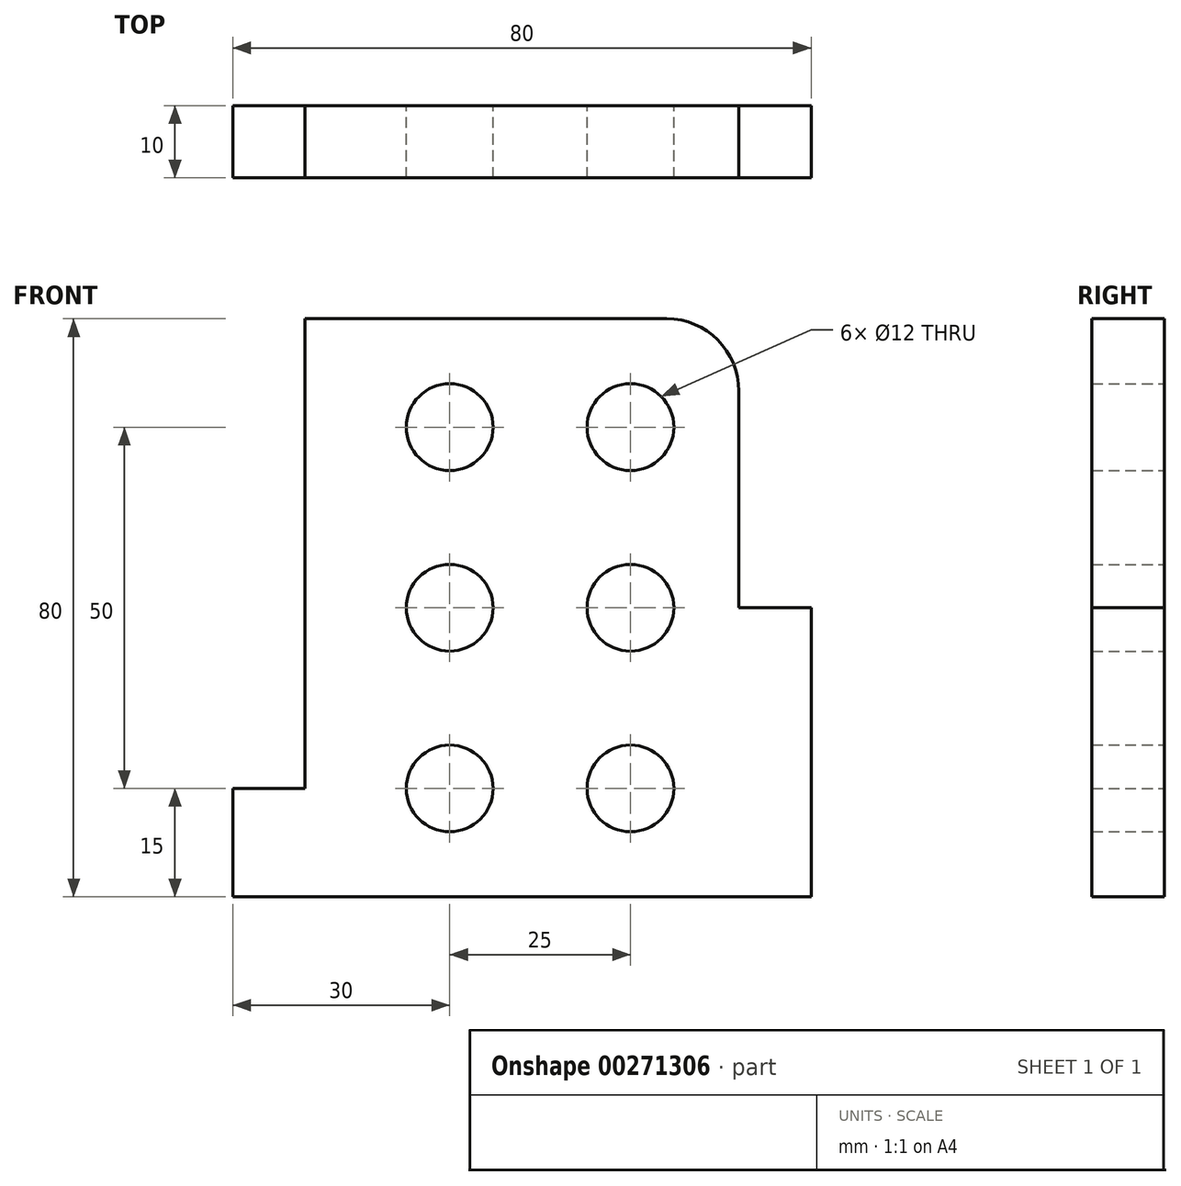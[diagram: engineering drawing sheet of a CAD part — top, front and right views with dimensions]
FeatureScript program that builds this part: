
annotation { "Feature Type Name" : "Feature", "Feature Type Description" : "" }
export const myFeature = defineFeature(function(context is Context, id is Id, definition is map)
    precondition{}
    {
        {
            var Q0;
            Q0=qCreatedBy(makeId("Front.planeOp"),FACE);
            var sketch = newSketch(context, id + "F0", { "sketchPlane" : qUnion([Q0])});
            skLineSegment(sketch, "E0", {"start": v(0, 0) * mm, "end": v(0, 15) * mm});
            skLineSegment(sketch, "E1", {"start": v(0, 15) * mm, "end": v(10, 15) * mm});
            skLineSegment(sketch, "E2", {"start": v(10, 15) * mm, "end": v(10, 80) * mm});
            skLineSegment(sketch, "E3", {"start": v(10, 80) * mm, "end": v(60, 80) * mm});
            skCircle(sketch, "E4", {"center": v(30, 15) * mm, "radius": 6 * mm});
            skCircle(sketch, "E5", {"center": v(55, 15) * mm, "radius": 6 * mm});
            skCircle(sketch, "E6", {"center": v(55, 40) * mm, "radius": 6 * mm});
            skCircle(sketch, "E7", {"center": v(30, 40) * mm, "radius": 6 * mm});
            skCircle(sketch, "E8", {"center": v(30, 65) * mm, "radius": 6 * mm});
            skCircle(sketch, "E9", {"center": v(55, 65) * mm, "radius": 6 * mm});
            skLineSegment(sketch, "E10", {"start": v(0, 0) * mm, "end": v(80, 0) * mm});
            skLineSegment(sketch, "E11", {"start": v(80, 0) * mm, "end": v(80, 40) * mm});
            skLineSegment(sketch, "E12", {"start": v(80, 40) * mm, "end": v(70, 40) * mm});
            skLineSegment(sketch, "E13", {"start": v(70, 40) * mm, "end": v(70, 70) * mm});
            skArc(sketch, "E14", {"start": v(70, 70) * mm, "mid": v(67.07, 77.07) * mm, "end": v(60, 80) * mm});
            skLineSegment(sketch, "E15.bottom", {"start": v(30, 65) * mm, "end": v(55, 65) * mm, "construction": true});
            skLineSegment(sketch, "E15.top", {"start": v(30, 15) * mm, "end": v(55, 15) * mm, "construction": true});
            skLineSegment(sketch, "E15.left", {"start": v(30, 65) * mm, "end": v(30, 15) * mm, "construction": true});
            skLineSegment(sketch, "E15.right", {"start": v(55, 65) * mm, "end": v(55, 15) * mm, "construction": true});
            skLineSegment(sketch, "E16", {"start": v(30, 40) * mm, "end": v(55, 40) * mm, "construction": true});
            skLineSegment(sketch, "E17", {"start": v(10, 15) * mm, "end": v(10, 65) * mm});
            skSolve(sketch);
        }
        {
            var Q0;
            Q0=makeQuery(id+"F0.imprint","IMPRINT",FACE,{"disambiguationData":[TD([[makeQuery(id+"F0.imprint","IMPRINT",EDGE,{"derivedFrom":sQuery(id+"F0.wireOp",EDGE,"E0")}),-1.0]])]});
            extrude(context, id + "F1", {"entities" : qUnion([Q0]), "depth" : 10 * mm});
        }
    });
